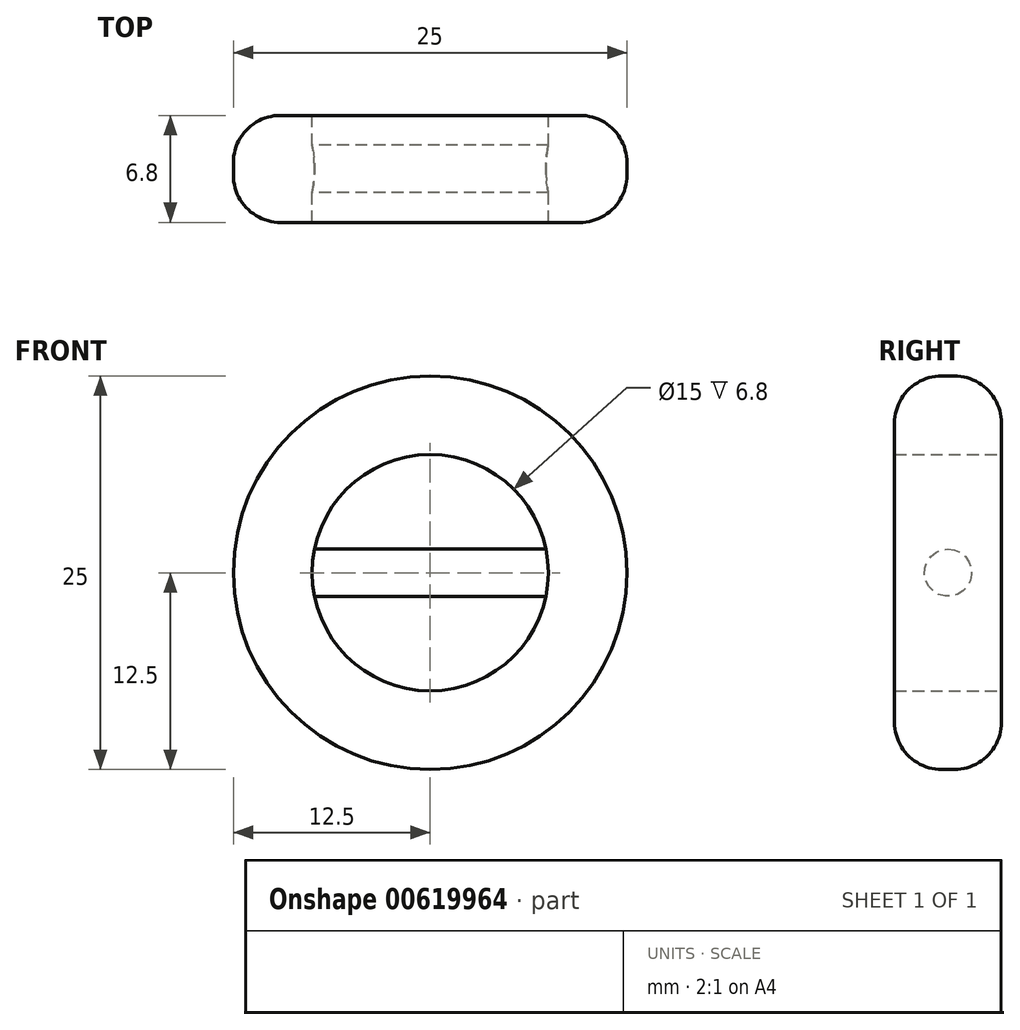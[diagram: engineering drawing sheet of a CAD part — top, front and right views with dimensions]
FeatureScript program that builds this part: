
annotation { "Feature Type Name" : "Feature", "Feature Type Description" : "" }
export const myFeature = defineFeature(function(context is Context, id is Id, definition is map)
    precondition{}
    {
        {
            var Q0;
            Q0=qCreatedBy(makeId("Front.planeOp"),FACE);
            var sketch = newSketch(context, id + "F0", { "sketchPlane" : qUnion([Q0])});
            skPoint(sketch, "E0.middle", {"position": v(0, 0) * mm});
            skCircle(sketch, "E1", {"center": v(0, 0) * mm, "radius": 7.5 * mm});
            skCircle(sketch, "E2", {"center": v(0, 0) * mm, "radius": 12.5 * mm});
            skSolve(sketch);
        }
        {
            var Q0;
            Q0 = qSketchRegion(id + "F0", true);
            extrude(context, id + "F1", {"entities" : qUnion([Q0]), "depth" : 6.8 * mm, "offsetDistance" : 25 * mm, "symmetric" : true});
        }
        {
            var Q0;
            Q0=makeQuery(id+"F1.opExtrude","CAP_EDGE",EDGE,{"disambiguationData":[OSD([sQuery(id+"F0.wireOp",EDGE,"E2")])],"isStart":true});
            var Q1;
            Q1=makeQuery(id+"F1.opExtrude","CAP_EDGE",EDGE,{"disambiguationData":[OSD([sQuery(id+"F0.wireOp",EDGE,"E2")])],"isStart":false});
            fillet(context, id + "F2", {"entities" : qUnion([Q0, Q1]), "radius" : 3 * mm, "tangentPropagation" : true, "allowEdgeOverflow" : false});
        }
        {
            var Q0;
            Q0=sQuery(id+"F0.wireOp",EDGE,"E1");
            extrude(context, id + "F3", {"bodyType" : ExtendedToolBodyType.SURFACE, "surfaceEntities" : qUnion([Q0]), "depth" : 6.8 * mm, "offsetDistance" : 25 * mm, "symmetric" : true});
        }
        {
            var Q0;
            Q0=qCreatedBy(makeId("Right.planeOp"),FACE);
            var sketch = newSketch(context, id + "F4", { "sketchPlane" : qUnion([Q0])});
            skCircle(sketch, "E3", {"center": v(0, 0) * mm, "radius": 1.5 * mm});
            skSolve(sketch);
        }
        {
            var Q0;
            Q0 = qSketchRegion(id + "F4", true);
            extrude(context, id + "F5", {"entities" : qUnion([Q0]), "operationType" : NewBodyOperationType.ADD, "depth" : 20 * mm, "offsetDistance" : 25 * mm, "symmetric" : true});
        }
    });
